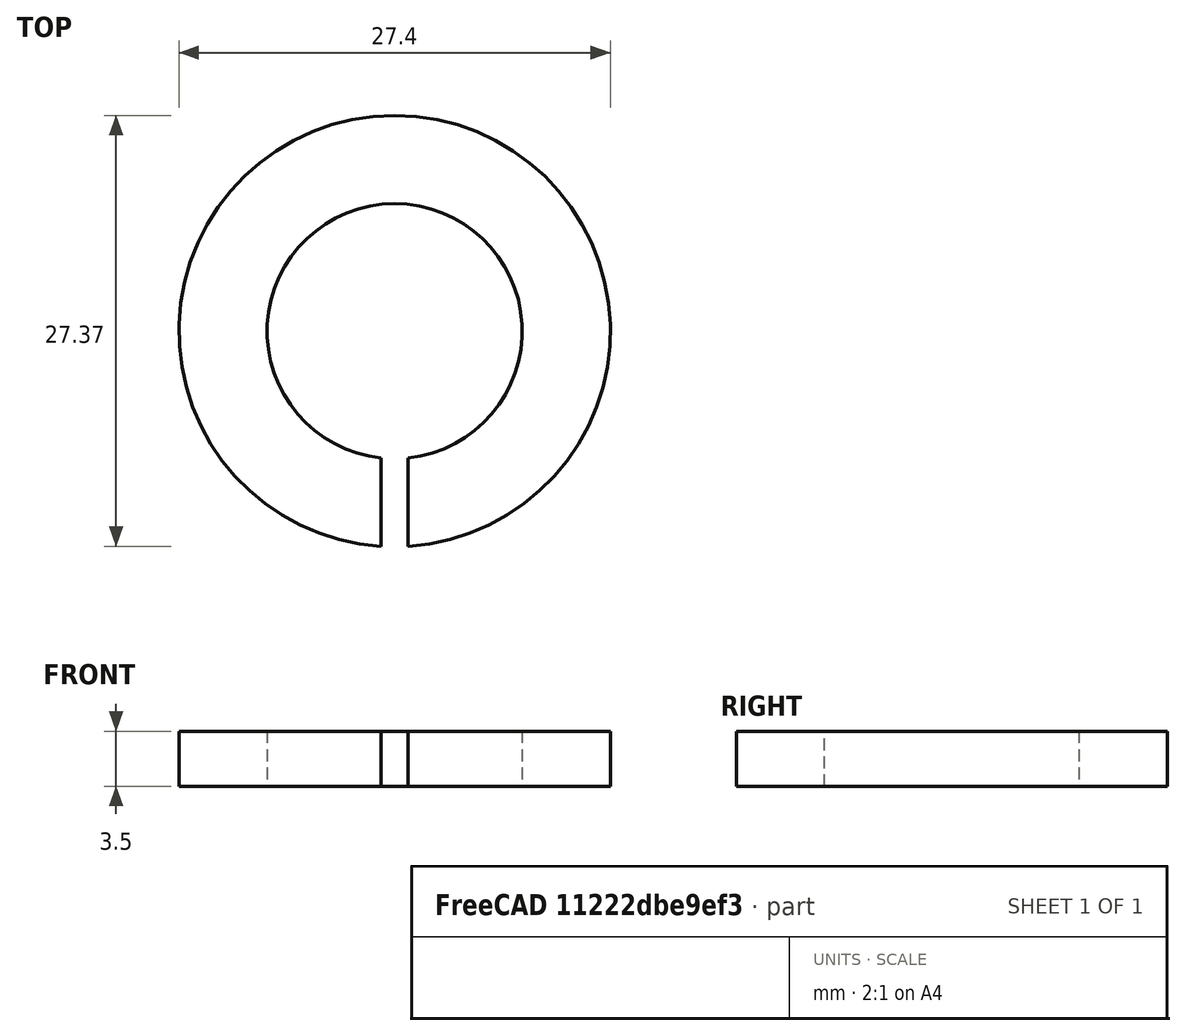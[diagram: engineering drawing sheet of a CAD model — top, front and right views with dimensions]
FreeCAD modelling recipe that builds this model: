
FCSTD DOCUMENT  (FreeCAD 0.15R4651 (Git))
Label: Federring_DIN127-A16
License: All rights reserved
LicenseURL: http://de.wikipedia.org/wiki/Alle_Rechte_vorbehalten
objects: Sketcher::SketchObject×1, PartDesign::Pad×1
note: 3 computed .brp shape members not serialized (recipe doc carries the construction recipe); baked Part::Feature solids carry a one-line shape summary decoded from their .brp

FEATURE [Sketcher::SketchObject] Sketch
  sketch-geometry (4):
    g0: ArcOfCircle CenterX=0 CenterY=0 CenterZ=0 NormalX=0 NormalY=0 NormalZ=1 Radius=8.1 StartAngle=4.81752 EndAngle=10.8904
    g1: ArcOfCircle CenterX=0 CenterY=0 CenterZ=0 NormalX=0 NormalY=0 NormalZ=1 Radius=13.7 StartAngle=4.77447 EndAngle=10.9335
    g2: LineSegment StartX=0.85 StartY=-8.05528 StartZ=0 EndX=0.85 EndY=-13.6736 EndZ=0
    g3: LineSegment StartX=-0.85 StartY=-13.6736 StartZ=0 EndX=-0.85 EndY=-8.05528 EndZ=0
  constraints (12):
    c: Coincident(g0,g-1)
    c: Coincident(g1,g-1)
    c: Vertical(g2)
    c: Vertical(g3)
    c: Coincident(g0,g2)
    c: Coincident(g0,g3)
    c: Coincident(g1,g2)
    c: Coincident(g1,g3)
    c: Symmetric(g1,g1,g-2)
    c: Radius(g0) = 8.1
    c: Radius(g1) = 13.7
    c: DistanceX(g1,g1) = -1.7
FEATURE [PartDesign::Pad] Pad  label="Federring DIN 127-A 16 #"
  Length = 3.5
  Length2 = 100
  Midplane = true
  Sketch = -> Sketch
  Type = 0
